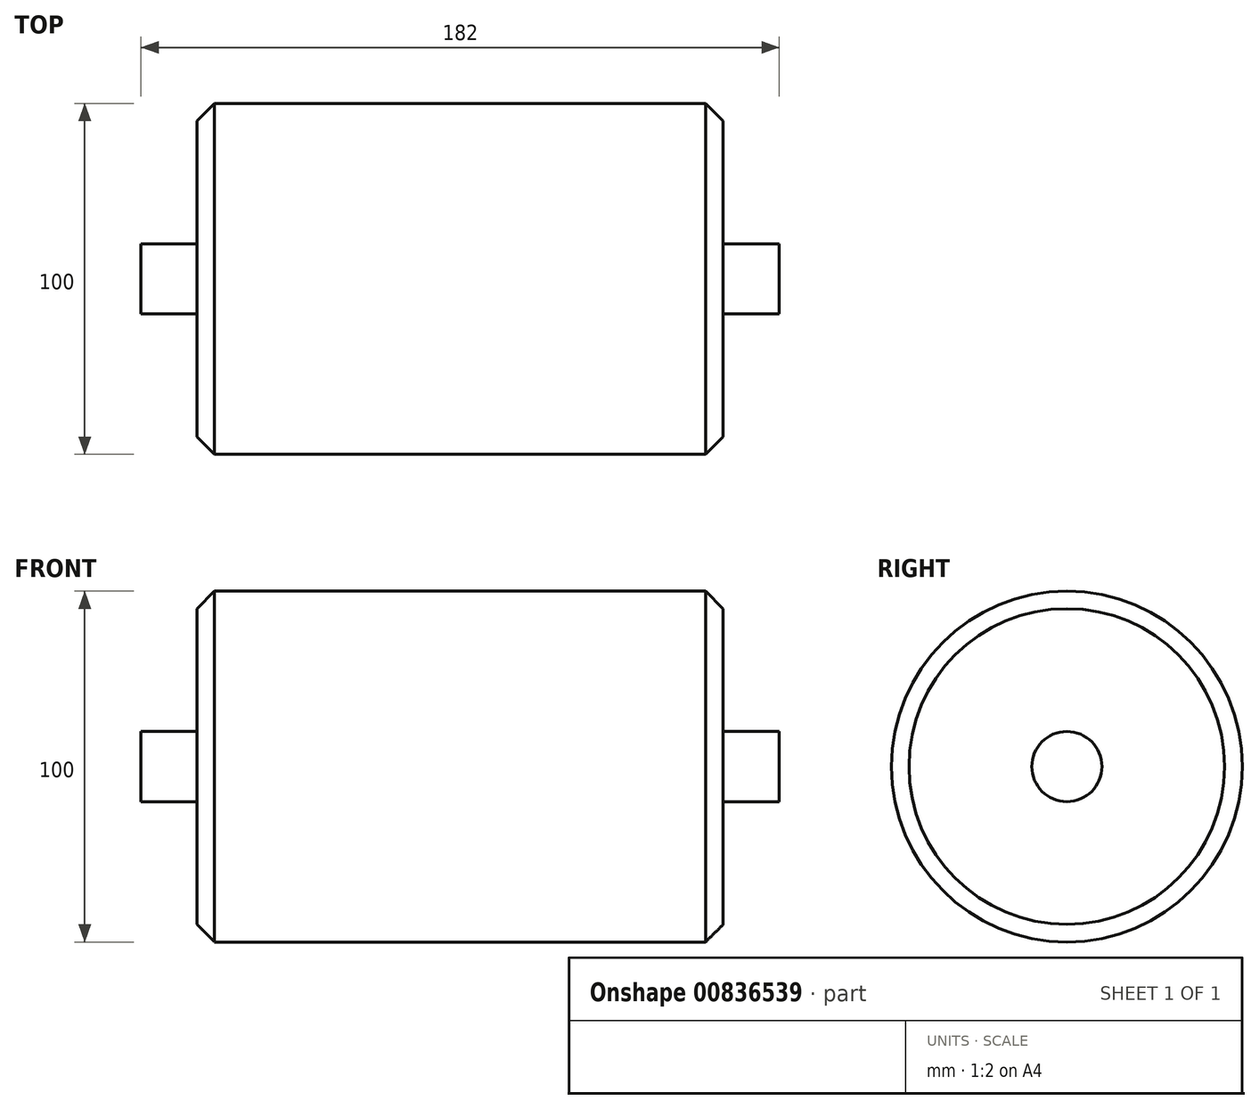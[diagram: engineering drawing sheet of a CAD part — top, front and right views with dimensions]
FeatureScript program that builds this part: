
annotation { "Feature Type Name" : "Feature", "Feature Type Description" : "" }
export const myFeature = defineFeature(function(context is Context, id is Id, definition is map)
    precondition{}
    {
        {
            var Q0;
            Q0=qCreatedBy(makeId("Top.planeOp"),FACE);
            var sketch = newSketch(context, id + "F0", { "sketchPlane" : qUnion([Q0])});
            skLineSegment(sketch, "E0.bottom", {"start": v(75, 0) * mm, "end": v(-75, 0) * mm});
            skLineSegment(sketch, "E0.top", {"start": v(75, 50) * mm, "end": v(-75, 50) * mm});
            skLineSegment(sketch, "E0.left", {"start": v(75, 0) * mm, "end": v(75, 50) * mm});
            skLineSegment(sketch, "E0.right", {"start": v(-75, 0) * mm, "end": v(-75, 50) * mm});
            skPoint(sketch, "E0.middle", {"position": v(0, 25) * mm});
            skLineSegment(sketch, "E1.bottom", {"start": v(75, 0) * mm, "end": v(91, 0) * mm});
            skLineSegment(sketch, "E1.top", {"start": v(75, 10) * mm, "end": v(91, 10) * mm});
            skLineSegment(sketch, "E1.left", {"start": v(75, 0) * mm, "end": v(75, 10) * mm});
            skLineSegment(sketch, "E1.right", {"start": v(91, 0) * mm, "end": v(91, 10) * mm});
            skLineSegment(sketch, "E2.bottom", {"start": v(-75, 0) * mm, "end": v(-91, 0) * mm});
            skLineSegment(sketch, "E2.top", {"start": v(-75, 10) * mm, "end": v(-91, 10) * mm});
            skLineSegment(sketch, "E2.left", {"start": v(-75, 0) * mm, "end": v(-75, 10) * mm});
            skLineSegment(sketch, "E2.right", {"start": v(-91, 0) * mm, "end": v(-91, 10) * mm});
            skSolve(sketch);
        }
        {
            var Q0;
            Q0=makeQuery(id+"F0.imprint","IMPRINT",FACE,{"disambiguationData":[TD([[makeQuery(id+"F0.imprint","IMPRINT",EDGE,{"derivedFrom":sQuery(id+"F0.wireOp",EDGE,"E2.bottom")}),-1.0]])]});
            var Q1;
            Q1=makeQuery(id+"F0.imprint","IMPRINT",FACE,{"disambiguationData":[TD([[makeQuery(id+"F0.imprint","IMPRINT",EDGE,{"derivedFrom":sQuery(id+"F0.wireOp",EDGE,"E0.bottom")}),-1.0]])]});
            var Q2;
            Q2=makeQuery(id+"F0.imprint","IMPRINT",FACE,{"disambiguationData":[TD([[makeQuery(id+"F0.imprint","IMPRINT",EDGE,{"derivedFrom":sQuery(id+"F0.wireOp",EDGE,"E1.bottom")}),1.0]])]});
            var Q3;
            Q3=sQuery(id+"F0.wireOp",EDGE,"E0.bottom");
            revolve(context, id + "F1", {"surfaceOperationType" : NewSurfaceOperationType.NEW, "entities" : qUnion([Q0, Q1, Q2]), "axis" : qUnion([Q3]), "revolveType" : RevolveType.FULL});
        }
        {
            var Q0;
            Q0=makeQuery(id+"F1.opRevolve","SWEPT_EDGE",EDGE,{"disambiguationData":[OSD([sQuery(id+"F0.wireOp",EDGE,"E0.top"),sQuery(id+"F0.wireOp",EDGE,"E0.right")])]});
            var Q1;
            Q1=makeQuery(id+"F1.opRevolve","SWEPT_EDGE",EDGE,{"disambiguationData":[OSD([sQuery(id+"F0.wireOp",EDGE,"E0.top"),sQuery(id+"F0.wireOp",EDGE,"E0.left")])]});
            chamfer(context, id + "F2", {"entities" : qUnion([Q0, Q1]), "width" : 5 * mm, "tangentPropagation" : true});
        }
    });
